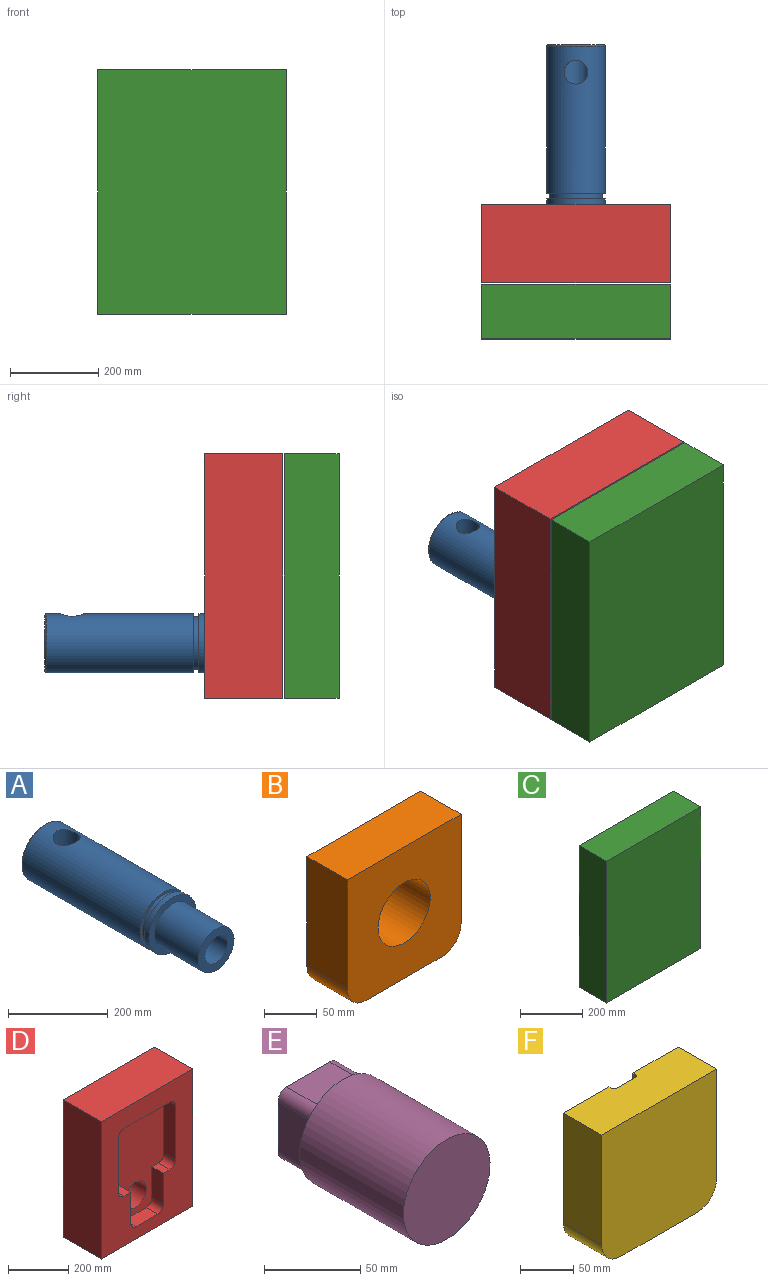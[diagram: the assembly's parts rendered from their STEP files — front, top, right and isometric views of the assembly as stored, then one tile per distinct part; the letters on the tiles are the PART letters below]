
ASSEMBLY  parts=6 mates=5
PART A: 12 faces, bbox 144.3x485.8x144.3 mm
  f0: cylinder r=66.67mm len=333.38mm, axis (0,-1,0), area 137322.9mm2, adj f7,f8,f10
  f1: cylinder r=31.75mm len=485.78mm, axis (0,-1,0), area 94321.5mm2, adj f3,f6,f8
  f2: cylinder r=66.67mm len=133.35mm, axis (0,-1,0), area 5320.4mm2, adj f4,f11
  f3: plane 127x127mm, normal (0,1,0), area 9500.8mm2, adj f1,f7
  f4: plane 133.35x133.35mm, normal (0,-1,0), area 5858.8mm2, adj f2,f5
  f5: cylinder r=50.8mm len=123.83mm, axis (0,1,0), area 39523.2mm2, adj f4,f6
  f6: plane 101.6x101.6mm, normal (0,-1,0), area 4940.4mm2, adj f1,f5
  f7: torus R=63.5mm, axis (0,-1,0), area 2053.2mm2, adj f0,f3
  f8: cylinder r=26.99mm len=53.98mm, axis (0,0,1), area 6616.2mm2, adj f0,f1
  f9: cylinder r=60.32mm len=120.65mm, axis (0,-1,0), area 4813.7mm2, adj f10,f11
  f10: plane 133.35x133.35mm, normal (0,-1,0), area 2533.5mm2, adj f0,f9
  f11: plane 133.35x133.35mm, normal (0,1,0), area 2533.5mm2, adj f2,f9
PART B: 9 faces, bbox 152.4x54x152.4 mm
  f0: plane 127x53.98mm, normal (1,0,0), area 6854.8mm2, adj f1,f4,f6,f8
  f1: plane 152.4x53.98mm, normal (0,0,1), area 8225.8mm2, adj f0,f2,f4,f8
  f2: plane 127x53.98mm, normal (-1,0,0), area 6854.8mm2, adj f1,f4,f5,f8
  f3: plane 101.6x53.98mm, normal (0,0,-1), area 5483.9mm2, adj f4,f5,f6,f8
  f4: plane 152.4x152.4mm, normal (0,-1,0), area 19116.9mm2, adj f0,f1,f2,f3,f5,f6,f7
  f5: cylinder r=25.4mm len=53.98mm, axis (0,1,0), area 2153.5mm2, adj f2,f3,f4,f8
  f6: cylinder r=25.4mm len=53.98mm, axis (0,-1,0), area 2153.5mm2, adj f0,f3,f4,f8
  f7: cylinder r=34.92mm len=69.85mm, axis (0,-1,0), area 11844.3mm2, adj f4,f8
  f8: plane 152.4x152.4mm, normal (0,1,0), area 19116.9mm2, adj f0,f1,f2,f3,f5,f6,f7
PART C: 21 faces, bbox 428.6x123.8x555.6 mm
  f0: plane 555.63x428.63mm, normal (0,1,0), area 142756.2mm2, adj f1,f2,f3,f4,f6,f7,f8,f9
  f1: plane 428.63x123.83mm, normal (0,0,-1), area 53074.5mm2, adj f0,f2,f4,f5
  f2: plane 555.63x123.83mm, normal (1,0,0), area 68800.3mm2, adj f0,f1,f3,f5
  f3: plane 428.63x123.83mm, normal (0,0,1), area 53074.5mm2, adj f0,f2,f4,f5
  f4: plane 555.63x123.83mm, normal (-1,0,0), area 68800.3mm2, adj f0,f1,f3,f5
  f5: plane 555.63x428.63mm, normal (0,-1,0), area 238154.8mm2, adj f1,f2,f3,f4
  f6: plane 127x50.8mm, normal (-1,0,0), area 6451.6mm2, adj f0,f7,f15,f16
  f7: plane 50.8x31.75mm, normal (0,0,1), area 1612.9mm2, adj f0,f6,f16,f17
  f8: plane 222.93x50.8mm, normal (-1,0,0), area 11324.8mm2, adj f0,f16,f17,f18
  f9: plane 215.9x50.8mm, normal (0,0,-1), area 10967.7mm2, adj f0,f16,f18,f19
  f10: plane 222.93x50.8mm, normal (1,0,0), area 11324.8mm2, adj f0,f16,f19,f20
  f11: plane 50.8x31.75mm, normal (0,0,1), area 1612.9mm2, adj f0,f12,f16,f20
  f12: plane 127x50.8mm, normal (1,0,0), area 6451.6mm2, adj f0,f11,f13,f16
  f13: cylinder r=25.4mm len=50.8mm, axis (0,1,0), area 2026.8mm2, adj f0,f12,f14,f16
  f14: plane 101.6x50.8mm, normal (0,0,1), area 5161.3mm2, adj f0,f13,f15,f16
  f15: cylinder r=25.4mm len=50.8mm, axis (0,1,0), area 2026.8mm2, adj f0,f6,f14,f16
  f16: plane 426.13x266.7mm, normal (0,1,0), area 95398.5mm2, adj f6,f7,f8,f9,f10,f11,f12,f13
  f17: cylinder r=25.4mm len=50.8mm, axis (0,-1,0), area 2026.8mm2, adj f0,f7,f8,f16
  f18: cylinder r=25.4mm len=50.8mm, axis (0,1,0), area 2026.8mm2, adj f0,f8,f9,f16
  f19: cylinder r=25.4mm len=50.8mm, axis (0,-1,0), area 2026.8mm2, adj f0,f9,f10,f16
  f20: cylinder r=25.4mm len=50.8mm, axis (0,1,0), area 2026.8mm2, adj f0,f10,f11,f16
PART D: 22 faces, bbox 428.6x177.8x555.6 mm
  f0: cylinder r=50.8mm len=123.83mm, axis (0,-1,0), area 39523.2mm2, adj f20,f21
  f1: plane 555.63x428.63mm, normal (0,-1,0), area 142754.4mm2, adj f2,f3,f4,f5,f6,f7,f8,f9
  f2: plane 428.63x177.8mm, normal (0,0,-1), area 76209.5mm2, adj f1,f3,f5,f20
  f3: plane 555.63x177.8mm, normal (1,0,0), area 98790.1mm2, adj f1,f2,f4,f20
  f4: plane 428.63x177.8mm, normal (0,0,1), area 76209.5mm2, adj f1,f3,f5,f20
  f5: plane 555.63x177.8mm, normal (-1,0,0), area 98790.1mm2, adj f1,f2,f4,f20
  f6: plane 53.98x31.75mm, normal (0,0,1), area 1713.7mm2, adj f1,f7,f19,f21
  f7: cylinder r=25.4mm len=53.98mm, axis (0,-1,0), area 2153.5mm2, adj f1,f6,f8,f21
  f8: plane 222.94x53.98mm, normal (-1,0,0), area 12033mm2, adj f1,f7,f9,f21
  f9: cylinder r=25.4mm len=53.98mm, axis (0,-1,0), area 2153.5mm2, adj f1,f8,f10,f21
  f10: plane 215.9x53.98mm, normal (0,0,-1), area 11653.2mm2, adj f1,f9,f11,f21
  f11: cylinder r=25.4mm len=53.98mm, axis (0,-1,0), area 2153.5mm2, adj f1,f10,f12,f21
  f12: plane 222.94x53.98mm, normal (1,0,0), area 12033mm2, adj f1,f11,f13,f21
  f13: cylinder r=25.4mm len=53.98mm, axis (0,-1,0), area 2153.5mm2, adj f1,f12,f14,f21
  f14: plane 53.98x31.75mm, normal (0,0,1), area 1713.7mm2, adj f1,f13,f15,f21
  f15: plane 127x53.98mm, normal (1,0,0), area 6854.8mm2, adj f1,f14,f16,f21
  f16: cylinder r=25.4mm len=53.98mm, axis (0,-1,0), area 2153.5mm2, adj f1,f15,f17,f21
  f17: plane 101.6x53.98mm, normal (0,0,1), area 5483.9mm2, adj f1,f16,f18,f21
  f18: cylinder r=25.4mm len=53.98mm, axis (0,-1,0), area 2153.5mm2, adj f1,f17,f19,f21
  f19: plane 127x53.98mm, normal (-1,0,0), area 6854.8mm2, adj f1,f6,f18,f21
  f20: plane 555.63x428.63mm, normal (0,1,0), area 230047.4mm2, adj f0,f2,f3,f4,f5
  f21: plane 426.14x266.7mm, normal (0,-1,0), area 87293.1mm2, adj f0,f6,f7,f8,f9,f10,f11,f12
PART E: 14 faces, bbox 63.5x101.6x63.5 mm
  f0: cylinder r=31.75mm len=76.2mm, axis (0,-1,0), area 15201.2mm2, adj f1,f2
  f1: plane 63.5x63.5mm, normal (0,1,0), area 1225.7mm2, adj f0,f3,f4,f5,f6,f8,f9,f10
  f2: plane 63.5x63.5mm, normal (0,-1,0), area 3166.9mm2, adj f0
  f3: plane 31.75x25.4mm, normal (-1,0,0), area 806.4mm2, adj f1,f7,f8,f11
  f4: plane 31.75x25.4mm, normal (0,0,1), area 806.4mm2, adj f1,f7,f8,f9
  f5: plane 31.75x25.4mm, normal (1,0,0), area 806.4mm2, adj f1,f7,f9,f10
  f6: plane 31.75x25.4mm, normal (0,0,-1), area 806.4mm2, adj f1,f7,f10,f11
  f7: plane 44.45x44.45mm, normal (0,1,0), area 801.1mm2, adj f3,f4,f5,f6,f8,f9,f10,f11
  f8: cylinder r=6.35mm len=25.4mm, axis (0,1,0), area 253.4mm2, adj f1,f3,f4,f7
  f9: cylinder r=6.35mm len=25.4mm, axis (0,-1,0), area 253.4mm2, adj f1,f4,f5,f7
  f10: cylinder r=6.35mm len=25.4mm, axis (0,1,0), area 253.4mm2, adj f1,f5,f6,f7
  f11: cylinder r=6.35mm len=25.4mm, axis (0,-1,0), area 253.4mm2, adj f1,f3,f6,f7
  f12: cylinder r=19.05mm len=79.5mm, axis (0,1,0), area 9516mm2, adj f7,f13
  f13: plane 38.1x38.1mm, normal (0,1,0), area 1140.1mm2, adj f12
PART F: 19 faces, bbox 152.4x50.8x152.4 mm
  f0: plane 152.4x50.8mm, normal (0,0,1), area 7544.6mm2, adj f1,f2,f4,f5,f8,f9,f10,f12
  f1: plane 127x50.8mm, normal (1,0,0), area 6451.6mm2, adj f0,f4,f5,f7
  f2: plane 127x50.8mm, normal (-1,0,0), area 6451.6mm2, adj f0,f4,f5,f6
  f3: plane 101.6x50.8mm, normal (0,0,-1), area 5161.3mm2, adj f4,f5,f6,f7
  f4: plane 152.4x152.4mm, normal (0,-1,0), area 22948.9mm2, adj f0,f1,f2,f3,f6,f7
  f5: plane 152.4x152.4mm, normal (0,1,0), area 19252.4mm2, adj f0,f1,f2,f3,f6,f7,f9,f10
  f6: cylinder r=25.4mm len=50.8mm, axis (0,-1,0), area 2026.8mm2, adj f2,f3,f4,f5
  f7: cylinder r=25.4mm len=50.8mm, axis (0,1,0), area 2026.8mm2, adj f1,f3,f4,f5
  f8: plane 98.43x44.45mm, normal (0,1,0), area 2957.7mm2, adj f0,f12,f15,f16,f17,f18
  f9: plane 54.9x3.18mm, normal (-1,0,0), area 174.3mm2, adj f0,f5,f14,f15
  f10: plane 54.9x3.18mm, normal (1,0,0), area 174.3mm2, adj f0,f5,f12,f13
  f11: cylinder r=25.4mm len=50.8mm, axis (0,1,0), area 389mm2, adj f5,f13,f14,f18
  f12: cylinder r=3.17mm len=54.9mm, axis (0,0,-1), area 273.8mm2, adj f0,f8,f10,f16
  f13: cylinder r=3.17mm len=3.18mm, axis (0,1,0), area 8.5mm2, adj f5,f10,f11,f16
  f14: cylinder r=3.17mm len=3.18mm, axis (0,1,0), area 8.5mm2, adj f5,f9,f11,f17
  f15: cylinder r=3.17mm len=54.9mm, axis (0,0,1), area 273.8mm2, adj f0,f8,f9,f17
  f16: torus R=6.35mm, axis (0,1,0), area 18.2mm2, adj f8,f12,f13,f18
  f17: torus R=6.35mm, axis (0,1,0), area 18.2mm2, adj f8,f14,f15,f18
  f18: torus R=22.23mm, axis (0,1,0), area 583.3mm2, adj f8,f11,f16,f17
PLACE A t=(-37.95,824.66,-138.77)mm
PLACE B t=(-37.95,847.52,44.11)mm
PLACE C t=(-37.95,643.3,-138.77)mm
PLACE D t=(-37.95,392.86,-138.77)mm
PLACE E t=(-37.95,662.59,-138.77)mm
PLACE F t=(-37.95,643.3,-138.77)mm
MATE fastened A.f0 <-> D.f0  axis (0,-1,0) through (-37.95,824.66,-138.77)mm
MATE fastened B.f4 <-> D.f1  axis (0,-1,0) through (-37.95,646.86,-214.97)mm
MATE slider C.f0 <-> D.f1  axis (0,1,0) through (-37.95,643.3,-264.18)mm
MATE slider E.f0 <-> A.f1  axis (0,-1,0) through (-37.95,662.59,-138.77)mm
MATE fastened C.f0 <-> F.f5  axis (0,1,0) through (38.25,643.3,-62.57)mm
